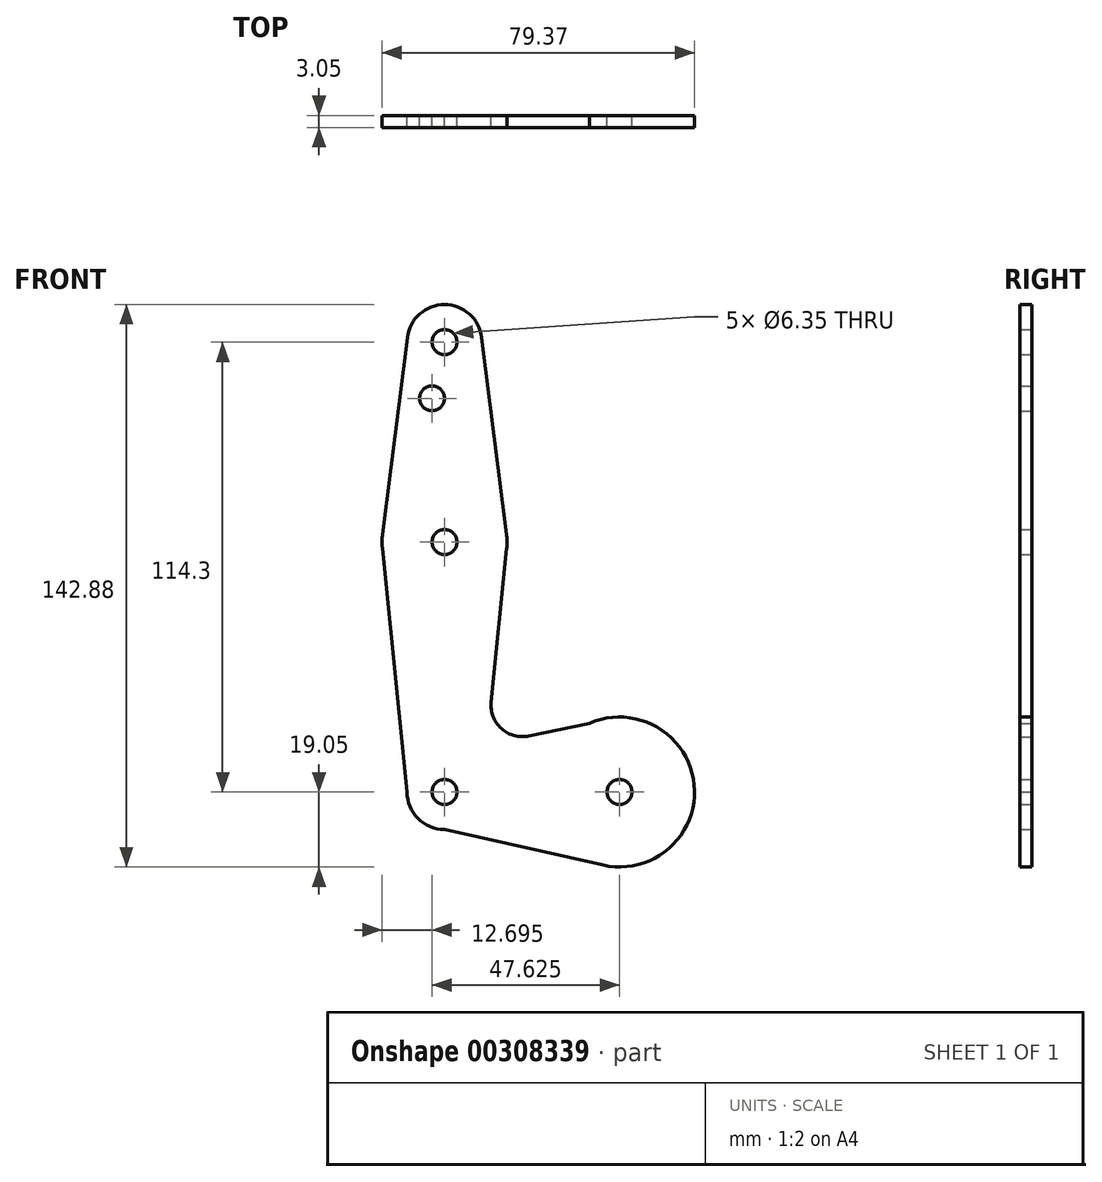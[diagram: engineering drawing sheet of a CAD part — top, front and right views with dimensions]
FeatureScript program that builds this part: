
annotation { "Feature Type Name" : "Feature", "Feature Type Description" : "" }
export const myFeature = defineFeature(function(context is Context, id is Id, definition is map)
    precondition{}
    {
        {
            var Q0;
            Q0=qCreatedBy(makeId("Front.planeOp"),FACE);
            var sketch = newSketch(context, id + "F0", { "sketchPlane" : qUnion([Q0])});
            skLineSegment(sketch, "E0", {"start": v(0, 0) * mm, "end": v(0, 114.3) * mm, "construction": true});
            skLineSegment(sketch, "E1", {"start": v(0, 0) * mm, "end": v(44.45, 0) * mm, "construction": true});
            skCircle(sketch, "E2", {"center": v(0, 114.3) * mm, "radius": 9.53 * mm});
            skCircle(sketch, "E3", {"center": v(0, 63.5) * mm, "radius": 15.88 * mm});
            skCircle(sketch, "E4", {"center": v(0, 0) * mm, "radius": 9.53 * mm});
            skCircle(sketch, "E5", {"center": v(44.45, 0) * mm, "radius": 19.05 * mm});
            skLineSegment(sketch, "E6", {"start": v(-15.75, 65.48) * mm, "end": v(-9.45, 115.5) * mm});
            skLineSegment(sketch, "E7", {"start": v(0, -9.52) * mm, "end": v(40.27, -18.59) * mm});
            skLineSegment(sketch, "E8", {"start": v(-9.52, 0) * mm, "end": v(-15.8, 61.9) * mm});
            skLineSegment(sketch, "E9", {"start": v(15.75, 65.48) * mm, "end": v(9.45, 115.5) * mm});
            skCircle(sketch, "E10", {"center": v(0, 114.3) * mm, "radius": 3.18 * mm});
            skCircle(sketch, "E11", {"center": v(0, 63.5) * mm, "radius": 3.18 * mm});
            skCircle(sketch, "E12", {"center": v(0, 0) * mm, "radius": 3.18 * mm});
            skCircle(sketch, "E13", {"center": v(44.45, 0) * mm, "radius": 3.18 * mm});
            skCircle(sketch, "E14", {"center": v(-3.18, 100.03) * mm, "radius": 3.18 * mm});
            skLineSegment(sketch, "E15", {"start": v(44.45, 19.05) * mm, "end": v(21.4, 14.22) * mm});
            skLineSegment(sketch, "E16", {"start": v(11.86, 22.8) * mm, "end": v(15.8, 61.91) * mm});
            skArc(sketch, "E17.filletArc", {"start": v(11.86, 22.8) * mm, "mid": v(14.46, 16.09) * mm, "end": v(21.4, 14.22) * mm});
            skSolve(sketch);
        }
        {
            var Q0;
            Q0 = qSketchRegion(id + "F0", true);
            extrude(context, id + "F1", {"entities" : qUnion([Q0]), "depth" : 3.05 * mm});
        }
    });
